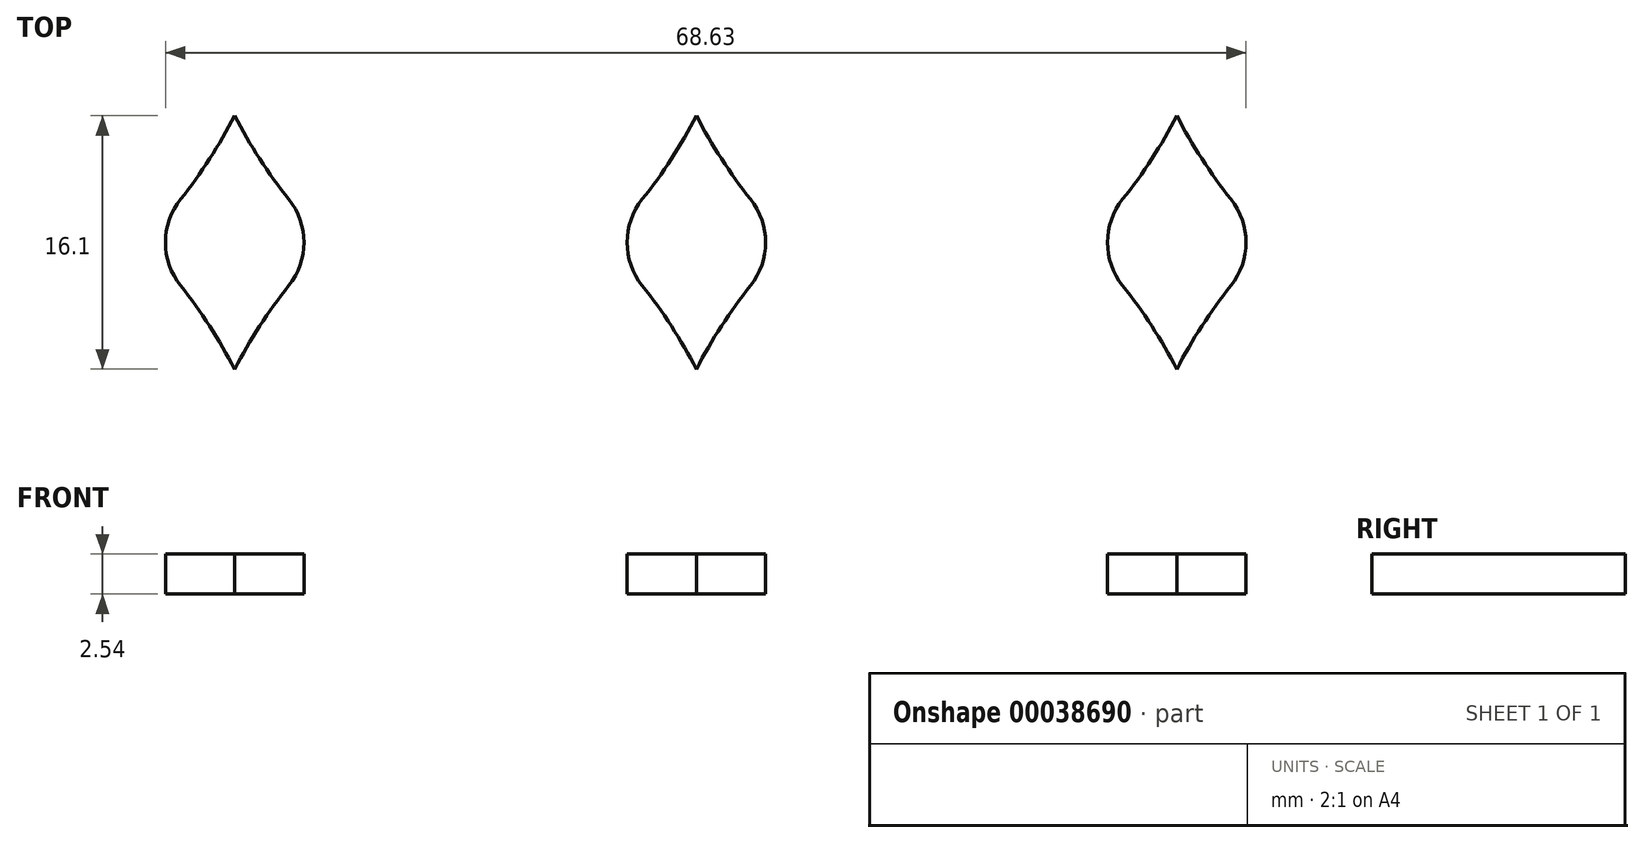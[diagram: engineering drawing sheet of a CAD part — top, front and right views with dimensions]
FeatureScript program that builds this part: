
annotation { "Feature Type Name" : "Feature", "Feature Type Description" : "" }
export const myFeature = defineFeature(function(context is Context, id is Id, definition is map)
    precondition{}
    {
        {
            var Q0;
            Q0=qCreatedBy(makeId("Top.planeOp"),FACE);
            var sketch = newSketch(context, id + "F0", { "sketchPlane" : qUnion([Q0])});
            skCircle(sketch, "E0", {"center": v(0, 0) * mm, "radius": 4.4 * mm});
            skArc(sketch, "E1", {"start": v(-3.44, 2.74) * mm, "mid": v(-1.59, 5.31) * mm, "end": v(0, 8.05) * mm});
            skArc(sketch, "E2.MirrorCS", {"start": v(3.44, 2.74) * mm, "mid": v(1.59, 5.31) * mm, "end": v(0, 8.05) * mm});
            skArc(sketch, "E3.MirrorCS", {"start": v(3.44, -2.74) * mm, "mid": v(1.59, -5.31) * mm, "end": v(0, -8.05) * mm});
            skArc(sketch, "E4.MirrorCS", {"start": v(-3.44, -2.74) * mm, "mid": v(-1.59, -5.31) * mm, "end": v(0, -8.05) * mm});
            skSolve(sketch);
        }
        {
            var Q0;
            {var subQ1=sQuery(id+"F0.wireOp",EDGE,"E1");Q0=makeQuery(id+"F0.imprint","IMPRINT",FACE,{"disambiguationData":[TD([[makeQuery(id+"F0.imprint","IMPRINT",EDGE,{"derivedFrom":subQ1}),-1.0]])]});}
            var Q1;
            {var subQ1=sQuery(id+"F0.wireOp",EDGE,"E3.MirrorCS");Q1=makeQuery(id+"F0.imprint","IMPRINT",FACE,{"disambiguationData":[TD([[makeQuery(id+"F0.imprint","IMPRINT",EDGE,{"derivedFrom":subQ1}),-1.0]])]});}
            var Q2;
            {var subQ0=sQuery(id+"F0.wireOp",EDGE,"E0");var subQ4=makeQuery(id+"F0.imprint","INTERSECT",VERTEX,{"derivedFrom":[subQ0,sQuery(id+"F0.wireOp",EDGE,"E1")]});Q2=makeQuery(id+"F0.imprint","IMPRINT",FACE,{"disambiguationData":[TD([[makeQuery(id+"F0.imprint","IMPRINT",EDGE,{"disambiguationData":[TD([[subQ4,1.0]])],"derivedFrom":subQ0}),1.0]])]});}
            extrude(context, id + "F1", {"entities" : qUnion([Q0, Q1, Q2]), "depth" : 2.54 * mm});
        }
        {
            var Q0;
            Q0=makeQuery(id+"F1.opExtrude","SWEPT_BODY",BODY,{"disambiguationData":[OSD([sQuery(id+"F0.wireOp",EDGE,"E0"),sQuery(id+"F0.wireOp",EDGE,"E1"),sQuery(id+"F0.wireOp",EDGE,"E2.MirrorCS"),sQuery(id+"F0.wireOp",EDGE,"E3.MirrorCS"),sQuery(id+"F0.wireOp",EDGE,"E4.MirrorCS")])]});
            transform(context, id + "F2", {"entities" : qUnion([Q0]), "transformType" : TransformType.TRANSLATION_3D, "dx" : 30.51 * mm, "dy" : 0 * mm, "dz" : 0 * mm, "makeCopy" : true});
        }
        {
            var Q0;
            Q0=makeQuery(id+"F1.opExtrude","SWEPT_BODY",BODY,{"disambiguationData":[OSD([sQuery(id+"F0.wireOp",EDGE,"E0"),sQuery(id+"F0.wireOp",EDGE,"E1"),sQuery(id+"F0.wireOp",EDGE,"E2.MirrorCS"),sQuery(id+"F0.wireOp",EDGE,"E3.MirrorCS"),sQuery(id+"F0.wireOp",EDGE,"E4.MirrorCS")])]});
            transform(context, id + "F3", {"entities" : qUnion([Q0]), "transformType" : TransformType.TRANSLATION_3D, "dx" : -29.33 * mm, "dy" : 0 * mm, "dz" : 0 * mm, "makeCopy" : true});
        }
    });
